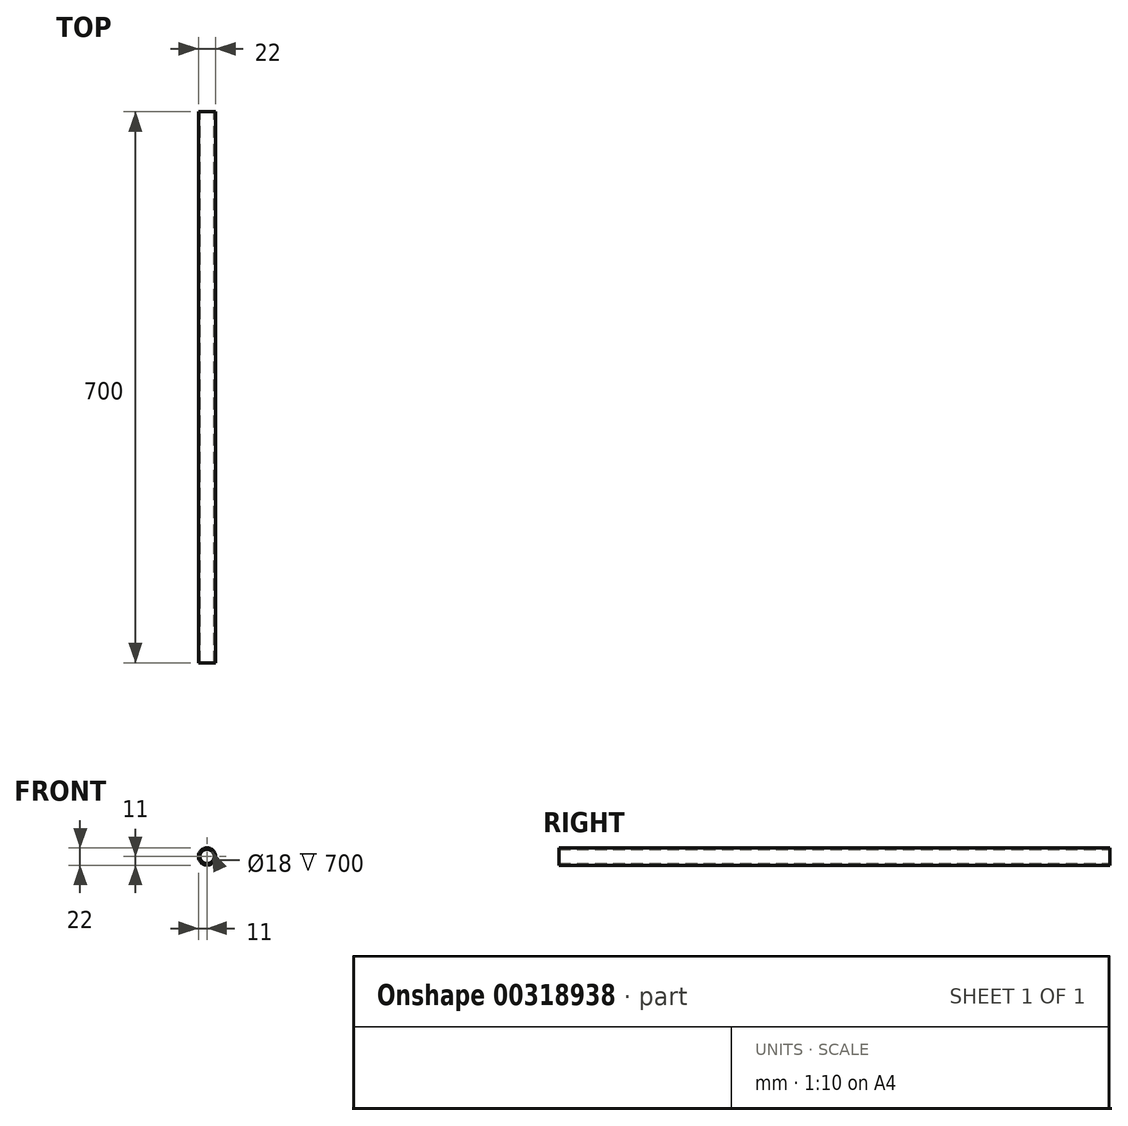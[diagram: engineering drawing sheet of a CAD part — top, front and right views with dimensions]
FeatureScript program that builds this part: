
annotation { "Feature Type Name" : "Feature", "Feature Type Description" : "" }
export const myFeature = defineFeature(function(context is Context, id is Id, definition is map)
    precondition{}
    {
        {
            var Q0;
            Q0=qCreatedBy(makeId("Front.planeOp"),FACE);
            var sketch = newSketch(context, id + "F0", { "sketchPlane" : qUnion([Q0])});
            skCircle(sketch, "E0", {"center": v(0, 0) * mm, "radius": 11 * mm});
            skCircle(sketch, "E1", {"center": v(0, 0) * mm, "radius": 9 * mm});
            skSolve(sketch);
        }
        {
            var Q0;
            Q0=makeQuery(id+"F0.imprint","IMPRINT",FACE,{"disambiguationData":[TD([[makeQuery(id+"F0.imprint","IMPRINT",EDGE,{"derivedFrom":sQuery(id+"F0.wireOp",EDGE,"E0")}),1.0]])]});
            var Q1;
            Q1=sQuery(id+"F0.wireOp",EDGE,"E0");
            extrude(context, id + "F1", {"entities" : qUnion([Q0]), "surfaceEntities" : qUnion([Q1]), "depth" : 700 * mm, "offsetDistance" : 25 * mm});
        }
    });
